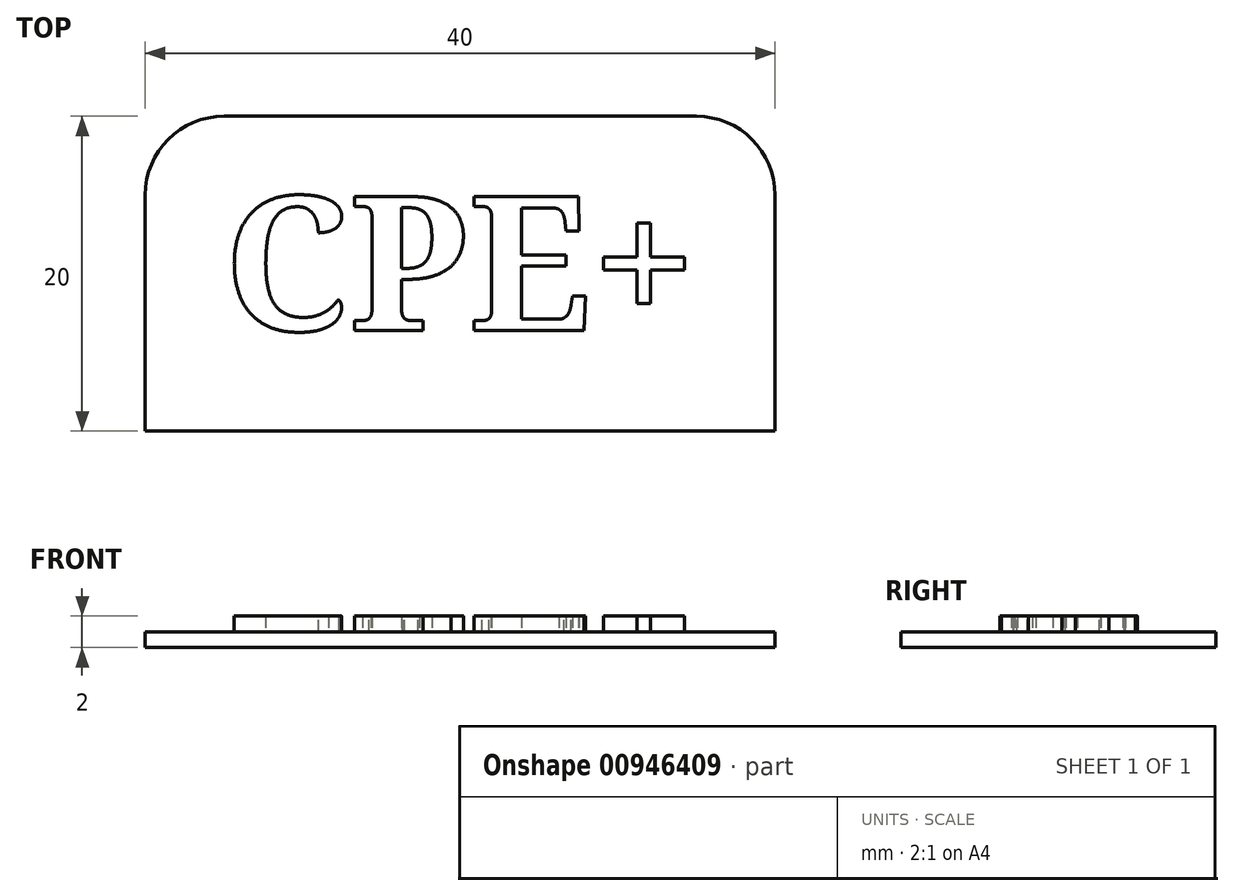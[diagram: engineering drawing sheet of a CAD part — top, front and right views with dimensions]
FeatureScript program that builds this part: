
annotation { "Feature Type Name" : "Feature", "Feature Type Description" : "" }
export const myFeature = defineFeature(function(context is Context, id is Id, definition is map)
    precondition{}
    {
        {
            var Q0;
            Q0=qCreatedBy(makeId("Top.planeOp"),FACE);
            var sketch = newSketch(context, id + "F0", { "sketchPlane" : qUnion([Q0])});
            skLineSegment(sketch, "E0.bottom", {"start": v(-20, 10) * mm, "end": v(20, 10) * mm});
            skLineSegment(sketch, "E0.top", {"start": v(-20, -10) * mm, "end": v(20, -10) * mm});
            skLineSegment(sketch, "E0.left", {"start": v(-20, 10) * mm, "end": v(-20, -10) * mm});
            skLineSegment(sketch, "E0.right", {"start": v(20, 10) * mm, "end": v(20, -10) * mm});
            skPoint(sketch, "E0.middle", {"position": v(0, 0) * mm});
            skSolve(sketch);
        }
        {
            var Q0;
            Q0=makeQuery(id+"F0.imprint","IMPRINT",FACE,{"disambiguationData":[TD([[makeQuery(id+"F0.imprint","IMPRINT",EDGE,{"derivedFrom":sQuery(id+"F0.wireOp",EDGE,"E0.bottom")}),-1.0]])]});
            extrude(context, id + "F1", {"entities" : qUnion([Q0]), "depth" : 1 * mm, "offsetDistance" : 25 * mm});
        }
        {
            var Q0;
            Q0=makeQuery(id+"F1.opExtrude","CAP_FACE",FACE,{"disambiguationData":[OSD([sQuery(id+"F0.wireOp",EDGE,"E0.bottom"),sQuery(id+"F0.wireOp",EDGE,"E0.top"),sQuery(id+"F0.wireOp",EDGE,"E0.left"),sQuery(id+"F0.wireOp",EDGE,"E0.right")])],"isStart":false});
            var sketch = newSketch(context, id + "F2", { "sketchPlane" : qUnion([Q0])});
            skText(sketch, "E1", { "text": "CPE+", "fontName": "NotoSerif-Bold.ttf"});
            const initialGuessF2  = {"E1": [-0.015, -0.00361, 1, 0, 0.00858]};
            skSetInitialGuess(sketch, initialGuessF2);
            skSolve(sketch);
        }
        {
            var Q0;
            Q0=qSketchRegion(id+"F2",true);
            extrude(context, id + "F3", {"entities" : qUnion([Q0]), "operationType" : NewBodyOperationType.ADD, "depth" : 1 * mm, "offsetDistance" : 25 * mm});
        }
        {
            var Q0;
            Q0=makeQuery(id+"F1.opExtrude","SWEPT_EDGE",EDGE,{"disambiguationData":[OSD([sQuery(id+"F0.wireOp",EDGE,"E0.bottom"),sQuery(id+"F0.wireOp",EDGE,"E0.left")])]});
            var Q1;
            Q1=makeQuery(id+"F1.opExtrude","SWEPT_EDGE",EDGE,{"disambiguationData":[OSD([sQuery(id+"F0.wireOp",EDGE,"E0.bottom"),sQuery(id+"F0.wireOp",EDGE,"E0.right")])]});
            fillet(context, id + "F4", {"entities" : qUnion([Q0, Q1]), "radius" : 5 * mm, "tangentPropagation" : true, "allowEdgeOverflow" : false});
        }
    });
